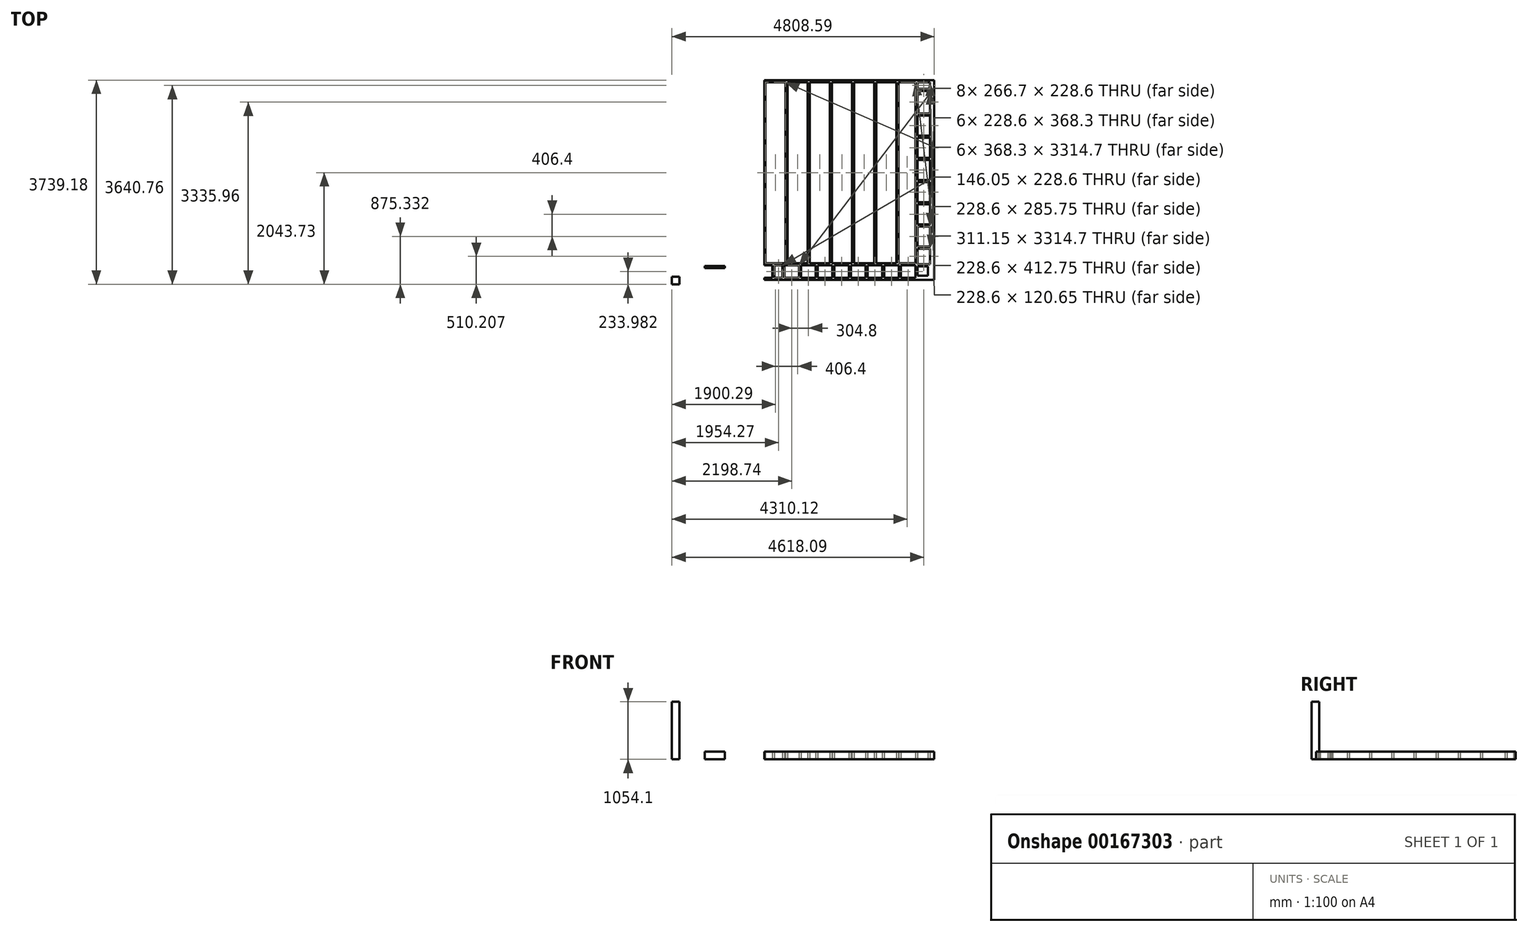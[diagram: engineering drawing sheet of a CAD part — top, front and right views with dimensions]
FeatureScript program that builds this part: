
annotation { "Feature Type Name" : "Feature", "Feature Type Description" : "" }
export const myFeature = defineFeature(function(context is Context, id is Id, definition is map)
    precondition{}
    {
        {
            var Q0;
            Q0=qCreatedBy(makeId("Top.planeOp"),FACE);
            var sketch = newSketch(context, id + "F0", { "sketchPlane" : qUnion([Q0])});
            skLineSegment(sketch, "E0.bottom", {"start": v(-2669.9, 3406.01) * mm, "end": v(403.5, 3406.01) * mm});
            skLineSegment(sketch, "E0.left", {"start": v(-2669.9, 3406.01) * mm, "end": v(-2669.9, 3367.91) * mm});
            skLineSegment(sketch, "E0.right", {"start": v(403.5, 3406.01) * mm, "end": v(403.5, -213.49) * mm});
            skPoint(sketch, "E1.orphan", {"position": v(238.4, 3406.01) * mm});
            skPoint(sketch, "E2.orphan", {"position": v(200.3, 3406.01) * mm});
            skLineSegment(sketch, "E3.0.3.0", {"start": v(136.8, 1170.81) * mm, "end": v(365.4, 1170.81) * mm});
            skLineSegment(sketch, "E3.0.3.1", {"start": v(136.8, 1132.71) * mm, "end": v(365.4, 1132.71) * mm});
            skLineSegment(sketch, "E3.0.4.0", {"start": v(136.8, 1577.21) * mm, "end": v(365.4, 1577.21) * mm});
            skLineSegment(sketch, "E3.0.6.0", {"start": v(136.8, 2390.01) * mm, "end": v(365.4, 2390.01) * mm});
            skLineSegment(sketch, "E3.0.6.1", {"start": v(136.8, 2351.91) * mm, "end": v(365.4, 2351.91) * mm});
            skLineSegment(sketch, "E4", {"start": v(-2669.9, -251.59) * mm, "end": v(403.5, -251.59) * mm});
            skLineSegment(sketch, "E5", {"start": v(-2669.9, -213.49) * mm, "end": v(-2523.85, -213.49) * mm});
            skLineSegment(sketch, "E6.trimOffspring", {"start": v(365.4, 65.91) * mm, "end": v(365.4, 34.16) * mm});
            skLineSegment(sketch, "E7.trimOffspring", {"start": v(136.8, -213.49) * mm, "end": v(403.5, -213.49) * mm});
            skLineSegment(sketch, "E8.trimOffspring", {"start": v(-2669.9, 15.11) * mm, "end": v(-2523.85, 15.11) * mm});
            skLineSegment(sketch, "E9.2.0.0", {"start": v(-1425.3, 15.11) * mm, "end": v(-1425.3, -213.49) * mm});
            skLineSegment(sketch, "E9.2.0.1", {"start": v(-1387.2, 15.11) * mm, "end": v(-1387.2, -213.49) * mm});
            skLineSegment(sketch, "E9.5.0.0", {"start": v(-206.1, 15.11) * mm, "end": v(-206.1, -213.49) * mm});
            skLineSegment(sketch, "E9.5.0.1", {"start": v(-168, 15.11) * mm, "end": v(-168, -213.49) * mm});
            skLineSegment(sketch, "E10.trimOffspring", {"start": v(-1996.8, 15.11) * mm, "end": v(-1730.1, 15.11) * mm});
            skLineSegment(sketch, "E11.trimOffspring", {"start": v(-1387.2, 15.11) * mm, "end": v(-1120.5, 15.11) * mm});
            skLineSegment(sketch, "E12.trimOffspring", {"start": v(-2671, 3367.91) * mm, "end": v(-2669.9, 3367.91) * mm});
            skLineSegment(sketch, "E13.trimOffspring", {"start": v(136.8, -3.94) * mm, "end": v(327.3, -3.94) * mm});
            skLineSegment(sketch, "E14.trimOffspring", {"start": v(365.4, -3.94) * mm, "end": v(365.4, -175.39) * mm});
            skLineSegment(sketch, "E15.trimOffspring", {"start": v(365.4, -213.49) * mm, "end": v(365.4, -213.49) * mm});
            skLineSegment(sketch, "E16.trimOffspring", {"start": v(365.4, -3.94) * mm, "end": v(365.4, -3.94) * mm});
            skLineSegment(sketch, "E17", {"start": v(-1996.8, 15.11) * mm, "end": v(-1996.8, -213.49) * mm});
            skLineSegment(sketch, "E18.trimOffspring", {"start": v(-2339.7, 15.11) * mm, "end": v(-2339.7, -213.49) * mm});
            skLineSegment(sketch, "E19.trimOffspring", {"start": v(-2301.6, 15.11) * mm, "end": v(-2301.6, -213.49) * mm});
            skLineSegment(sketch, "E20.trimOffspring", {"start": v(-2301.6, 15.11) * mm, "end": v(-2034.9, 15.11) * mm});
            skLineSegment(sketch, "E21.trimOffspring", {"start": v(-2034.9, 15.11) * mm, "end": v(-2034.9, -213.49) * mm});
            skLineSegment(sketch, "E22.trimOffspring", {"start": v(-1730.1, 15.11) * mm, "end": v(-1730.1, -213.49) * mm});
            skLineSegment(sketch, "E23.trimOffspring", {"start": v(-1692, 15.11) * mm, "end": v(-1692, -213.49) * mm});
            skLineSegment(sketch, "E24.trimOffspring", {"start": v(-1692, 15.11) * mm, "end": v(-1425.3, 15.11) * mm});
            skLineSegment(sketch, "E25.trimOffspring", {"start": v(-1120.5, 15.11) * mm, "end": v(-1120.5, -213.49) * mm});
            skLineSegment(sketch, "E26.trimOffspring", {"start": v(-1082.4, 15.11) * mm, "end": v(-815.7, 15.11) * mm});
            skLineSegment(sketch, "E27.trimOffspring", {"start": v(-1082.4, 15.11) * mm, "end": v(-1082.4, -213.49) * mm});
            skLineSegment(sketch, "E28.trimOffspring", {"start": v(-815.7, 15.11) * mm, "end": v(-815.7, -213.49) * mm});
            skLineSegment(sketch, "E29.trimOffspring", {"start": v(-777.6, 15.11) * mm, "end": v(-510.9, 15.11) * mm});
            skLineSegment(sketch, "E30.trimOffspring", {"start": v(-777.6, 15.11) * mm, "end": v(-777.6, -213.49) * mm});
            skLineSegment(sketch, "E31.trimOffspring", {"start": v(-510.9, 15.11) * mm, "end": v(-510.9, -213.49) * mm});
            skLineSegment(sketch, "E32.trimOffspring", {"start": v(-472.8, 15.11) * mm, "end": v(-206.1, 15.11) * mm});
            skLineSegment(sketch, "E33.trimOffspring", {"start": v(-472.8, 15.11) * mm, "end": v(-472.8, -213.49) * mm});
            skLineSegment(sketch, "E34.trimOffspring", {"start": v(-168, 15.11) * mm, "end": v(98.7, 15.11) * mm});
            skLineSegment(sketch, "E35.trimOffspring", {"start": v(98.7, 3367.91) * mm, "end": v(98.7, 53.21) * mm});
            skLineSegment(sketch, "E36.trimOffspring", {"start": v(136.8, 2796.41) * mm, "end": v(365.4, 2796.41) * mm});
            skLineSegment(sketch, "E37.trimOffspring", {"start": v(136.8, 2758.31) * mm, "end": v(365.4, 2758.31) * mm});
            skLineSegment(sketch, "E38.trimOffspring", {"start": v(136.8, 3367.91) * mm, "end": v(365.4, 3367.91) * mm});
            skLineSegment(sketch, "E39.trimOffspring", {"start": v(136.8, 3367.91) * mm, "end": v(136.8, 3247.26) * mm});
            skLineSegment(sketch, "E40.trimOffspring", {"start": v(136.8, 1983.61) * mm, "end": v(365.4, 1983.61) * mm});
            skLineSegment(sketch, "E41.trimOffspring", {"start": v(136.8, 1945.51) * mm, "end": v(365.4, 1945.51) * mm});
            skLineSegment(sketch, "E42.trimOffspring", {"start": v(136.8, 1539.11) * mm, "end": v(365.4, 1539.11) * mm});
            skLineSegment(sketch, "E43.trimOffspring", {"start": v(136.8, 1539.11) * mm, "end": v(136.8, 1170.81) * mm});
            skLineSegment(sketch, "E44.trimOffspring", {"start": v(365.4, 1539.11) * mm, "end": v(365.4, 1170.81) * mm});
            skLineSegment(sketch, "E45.trimOffspring", {"start": v(136.8, 1132.71) * mm, "end": v(136.8, 764.41) * mm});
            skLineSegment(sketch, "E46.trimOffspring", {"start": v(136.8, 764.41) * mm, "end": v(365.4, 764.41) * mm});
            skLineSegment(sketch, "E47.trimOffspring", {"start": v(136.8, 726.31) * mm, "end": v(365.4, 726.31) * mm});
            skLineSegment(sketch, "E48.trimOffspring", {"start": v(136.8, 726.31) * mm, "end": v(136.8, 358.01) * mm});
            skLineSegment(sketch, "E49.trimOffspring", {"start": v(136.8, 358.01) * mm, "end": v(365.4, 358.01) * mm});
            skLineSegment(sketch, "E50.trimOffspring", {"start": v(136.8, 319.91) * mm, "end": v(136.8, 53.21) * mm});
            skLineSegment(sketch, "E51.trimOffspring", {"start": v(136.8, 319.91) * mm, "end": v(365.4, 319.91) * mm});
            skLineSegment(sketch, "E52.trimOffspring", {"start": v(136.8, 34.16) * mm, "end": v(365.4, 34.16) * mm});
            skLineSegment(sketch, "E53.trimOffspring", {"start": v(136.8, 65.91) * mm, "end": v(136.8, 34.16) * mm});
            skLineSegment(sketch, "E54.trimOffspring", {"start": v(98.7, 15.11) * mm, "end": v(98.7, -213.49) * mm});
            skLineSegment(sketch, "E55.trimOffspring", {"start": v(136.8, -3.94) * mm, "end": v(136.8, -175.39) * mm});
            skLineSegment(sketch, "E56.trimOffspring", {"start": v(136.8, -213.49) * mm, "end": v(136.8, -213.49) * mm});
            skLineSegment(sketch, "E57.trimOffspring", {"start": v(365.4, 319.91) * mm, "end": v(365.4, 53.21) * mm});
            skLineSegment(sketch, "E58.trimOffspring", {"start": v(365.4, 726.31) * mm, "end": v(365.4, 358.01) * mm});
            skLineSegment(sketch, "E59.trimOffspring", {"start": v(365.4, 1132.71) * mm, "end": v(365.4, 764.41) * mm});
            skLineSegment(sketch, "E60.trimOffspring", {"start": v(365.4, 1945.51) * mm, "end": v(365.4, 1577.21) * mm});
            skLineSegment(sketch, "E61.trimOffspring", {"start": v(365.4, 2351.91) * mm, "end": v(365.4, 1983.61) * mm});
            skLineSegment(sketch, "E62.trimOffspring", {"start": v(365.4, 2758.31) * mm, "end": v(365.4, 2390.01) * mm});
            skLineSegment(sketch, "E63.trimOffspring", {"start": v(365.4, 3367.91) * mm, "end": v(365.4, 3247.26) * mm});
            skLineSegment(sketch, "E64.trimOffspring", {"start": v(-168, -213.49) * mm, "end": v(98.7, -213.49) * mm});
            skLineSegment(sketch, "E65.trimOffspring", {"start": v(-472.8, -213.49) * mm, "end": v(-206.1, -213.49) * mm});
            skLineSegment(sketch, "E66.trimOffspring", {"start": v(-777.6, -213.49) * mm, "end": v(-510.9, -213.49) * mm});
            skLineSegment(sketch, "E67.trimOffspring", {"start": v(-1082.4, -213.49) * mm, "end": v(-815.7, -213.49) * mm});
            skLineSegment(sketch, "E68.trimOffspring", {"start": v(-1387.2, -213.49) * mm, "end": v(-1120.5, -213.49) * mm});
            skLineSegment(sketch, "E69.trimOffspring", {"start": v(-1692, -213.49) * mm, "end": v(-1425.3, -213.49) * mm});
            skLineSegment(sketch, "E70.trimOffspring", {"start": v(-2301.6, -213.49) * mm, "end": v(-2034.9, -213.49) * mm});
            skLineSegment(sketch, "E71.trimOffspring", {"start": v(-2523.85, -213.49) * mm, "end": v(-2339.7, -213.49) * mm});
            skLineSegment(sketch, "E72.trimOffspring", {"start": v(-1996.8, -213.49) * mm, "end": v(-1730.1, -213.49) * mm});
            skLineSegment(sketch, "E73.trimOffspring", {"start": v(136.8, 3209.16) * mm, "end": v(365.4, 3209.16) * mm});
            skPoint(sketch, "E74.orphan", {"position": v(149.5, 3367.91) * mm});
            skLineSegment(sketch, "E75.trimOffspring", {"start": v(136.8, 3247.26) * mm, "end": v(365.4, 3247.26) * mm});
            skLineSegment(sketch, "E76.trimOffspring", {"start": v(136.8, 3209.16) * mm, "end": v(136.8, 2390.01) * mm});
            skLineSegment(sketch, "E77.trimOffspring", {"start": v(365.4, 3209.16) * mm, "end": v(365.4, 2796.41) * mm});
            skLineSegment(sketch, "E78.trimOffspring", {"start": v(136.8, 2351.91) * mm, "end": v(136.8, 1983.61) * mm});
            skLineSegment(sketch, "E79.trimOffspring", {"start": v(136.8, 1945.51) * mm, "end": v(136.8, 1577.21) * mm});
            skLineSegment(sketch, "E80.0", {"start": v(327.3, -3.94) * mm, "end": v(327.3, -175.39) * mm});
            skLineSegment(sketch, "E81.0", {"start": v(136.8, -175.39) * mm, "end": v(327.3, -175.39) * mm});
            skLineSegment(sketch, "E82.0", {"start": v(136.8, -213.49) * mm, "end": v(365.4, -213.49) * mm});
            skLineSegment(sketch, "E83.trimOffspring", {"start": v(365.4, -175.39) * mm, "end": v(365.4, -175.39) * mm});
            skLineSegment(sketch, "E84.trimOffspring", {"start": v(-2485.75, 15.11) * mm, "end": v(-2339.7, 15.11) * mm});
            skLineSegment(sketch, "E85.trimOffspring", {"start": v(-2485.75, 15.11) * mm, "end": v(-2485.75, -213.49) * mm});
            skLineSegment(sketch, "E86.trimOffspring", {"start": v(-2523.85, 15.11) * mm, "end": v(-2523.85, -213.49) * mm});
            skLineSegment(sketch, "E87", {"start": v(-2669.9, -213.49) * mm, "end": v(-2669.9, -251.59) * mm});
            skLineSegment(sketch, "E88", {"start": v(-2669.9, 53.21) * mm, "end": v(-2669.9, 15.11) * mm});
            skLineSegment(sketch, "E89.0", {"start": v(441.6, 3406.01) * mm, "end": v(441.6, -251.59) * mm});
            skLineSegment(sketch, "E90", {"start": v(403.5, 3406.01) * mm, "end": v(441.6, 3406.01) * mm});
            skLineSegment(sketch, "E91", {"start": v(403.5, -251.59) * mm, "end": v(441.6, -251.59) * mm});
            skLineSegment(sketch, "E92.0", {"start": v(-2671, 3406.01) * mm, "end": v(-2671, 3367.91) * mm});
            skLineSegment(sketch, "E93.0", {"start": v(-2650.85, 3367.91) * mm, "end": v(-2650.85, 53.21) * mm});
            skLineSegment(sketch, "E94", {"start": v(-2669.9, 53.21) * mm, "end": v(-2669.9, 3367.91) * mm});
            skLineSegment(sketch, "E95.trimOffspring", {"start": v(-2650.85, 3367.91) * mm, "end": v(-2282.55, 3367.91) * mm});
            skLineSegment(sketch, "E96", {"start": v(98.7, 53.21) * mm, "end": v(-2650.85, 53.21) * mm});
            skPoint(sketch, "E97.orphan", {"position": v(-2650.85, 15.11) * mm});
            skLineSegment(sketch, "E98.0", {"start": v(-2244.45, 3367.91) * mm, "end": v(-2244.45, 53.21) * mm});
            skLineSegment(sketch, "E99.0", {"start": v(-2282.55, 3367.91) * mm, "end": v(-2282.55, 53.21) * mm});
            skLineSegment(sketch, "E100.1.0.0", {"start": v(-1838.05, 3367.91) * mm, "end": v(-1838.05, 53.21) * mm});
            skLineSegment(sketch, "E100.1.0.1", {"start": v(-1876.15, 3367.91) * mm, "end": v(-1876.15, 53.21) * mm});
            skLineSegment(sketch, "E100.2.0.0", {"start": v(-1431.65, 3367.91) * mm, "end": v(-1431.65, 53.21) * mm});
            skLineSegment(sketch, "E100.2.0.1", {"start": v(-1469.75, 3367.91) * mm, "end": v(-1469.75, 53.21) * mm});
            skLineSegment(sketch, "E100.3.0.0", {"start": v(-1025.25, 3367.91) * mm, "end": v(-1025.25, 53.21) * mm});
            skLineSegment(sketch, "E100.3.0.1", {"start": v(-1063.35, 3367.91) * mm, "end": v(-1063.35, 53.21) * mm});
            skLineSegment(sketch, "E100.4.0.0", {"start": v(-618.85, 3367.91) * mm, "end": v(-618.85, 53.21) * mm});
            skLineSegment(sketch, "E100.4.0.1", {"start": v(-656.95, 3367.91) * mm, "end": v(-656.95, 53.21) * mm});
            skLineSegment(sketch, "E100.5.0.0", {"start": v(-212.45, 3367.91) * mm, "end": v(-212.45, 53.21) * mm});
            skLineSegment(sketch, "E100.5.0.1", {"start": v(-250.55, 3367.91) * mm, "end": v(-250.55, 53.21) * mm});
            skLineSegment(sketch, "E100.direction1", {"start": v(-2282.55, 53.21) * mm, "end": v(-1876.15, 53.21) * mm, "construction": true});
            skLineSegment(sketch, "E101.trimOffspring", {"start": v(-2244.45, 3367.91) * mm, "end": v(-1876.15, 3367.91) * mm});
            skLineSegment(sketch, "E102.trimOffspring", {"start": v(-1838.05, 3367.91) * mm, "end": v(-1469.75, 3367.91) * mm});
            skLineSegment(sketch, "E103.trimOffspring", {"start": v(-1431.65, 3367.91) * mm, "end": v(-1063.35, 3367.91) * mm});
            skLineSegment(sketch, "E104.trimOffspring", {"start": v(-1025.25, 3367.91) * mm, "end": v(-656.95, 3367.91) * mm});
            skLineSegment(sketch, "E105.trimOffspring", {"start": v(-618.85, 3367.91) * mm, "end": v(-250.55, 3367.91) * mm});
            skLineSegment(sketch, "E106.trimOffspring", {"start": v(-212.45, 3367.91) * mm, "end": v(98.7, 3367.91) * mm});
            skSolve(sketch);
        }
        {
            var Q0;
            {var subQ0=sQuery(id+"F0.wireOp",EDGE,"b4387343-3526-4506-bbcd-7e7664f48f6e.trimOffspring");Q0=makeQuery(id+"F0.imprint","IMPRINT",FACE,{"disambiguationData":[TD([[makeQuery(id+"F0.imprint","IMPRINT",EDGE,{"derivedFrom":subQ0}),1.0]])]});}
            var Q1;
            {var subQ0=sQuery(id+"F0.wireOp",EDGE,"E3.0.1.0");Q1=makeQuery(id+"F0.imprint","IMPRINT",FACE,{"disambiguationData":[TD([[makeQuery(id+"F0.imprint","IMPRINT",EDGE,{"derivedFrom":subQ0}),-1.0]])]});}
            var Q2;
            {var subQ0=sQuery(id+"F0.wireOp",EDGE,"E3.0.2.0");Q2=makeQuery(id+"F0.imprint","IMPRINT",FACE,{"disambiguationData":[TD([[makeQuery(id+"F0.imprint","IMPRINT",EDGE,{"derivedFrom":subQ0}),-1.0]])]});}
            var Q3;
            {var subQ0=sQuery(id+"F0.wireOp",EDGE,"E3.0.3.0");Q3=makeQuery(id+"F0.imprint","IMPRINT",FACE,{"disambiguationData":[TD([[makeQuery(id+"F0.imprint","IMPRINT",EDGE,{"derivedFrom":subQ0}),-1.0]])]});}
            var Q4;
            {var subQ0=sQuery(id+"F0.wireOp",EDGE,"E3.0.4.0");Q4=makeQuery(id+"F0.imprint","IMPRINT",FACE,{"disambiguationData":[TD([[makeQuery(id+"F0.imprint","IMPRINT",EDGE,{"derivedFrom":subQ0}),-1.0]])]});}
            var Q5;
            {var subQ0=sQuery(id+"F0.wireOp",EDGE,"E3.0.5.0");Q5=makeQuery(id+"F0.imprint","IMPRINT",FACE,{"disambiguationData":[TD([[makeQuery(id+"F0.imprint","IMPRINT",EDGE,{"derivedFrom":subQ0}),-1.0]])]});}
            var Q6;
            {var subQ0=sQuery(id+"F0.wireOp",EDGE,"E3.0.6.0");Q6=makeQuery(id+"F0.imprint","IMPRINT",FACE,{"disambiguationData":[TD([[makeQuery(id+"F0.imprint","IMPRINT",EDGE,{"derivedFrom":subQ0}),-1.0]])]});}
            var Q7;
            {var subQ0=sQuery(id+"F0.wireOp",EDGE,"E3.0.7.0");Q7=makeQuery(id+"F0.imprint","IMPRINT",FACE,{"disambiguationData":[TD([[makeQuery(id+"F0.imprint","IMPRINT",EDGE,{"derivedFrom":subQ0}),-1.0]])]});}
            var Q8;
            {var subQ0=sQuery(id+"F0.wireOp",EDGE,"E3.0.8.0");Q8=makeQuery(id+"F0.imprint","IMPRINT",FACE,{"disambiguationData":[TD([[makeQuery(id+"F0.imprint","IMPRINT",EDGE,{"derivedFrom":subQ0}),-1.0]])]});}
            var Q9;
            Q9=makeQuery(id+"F0.imprint","IMPRINT",FACE,{"disambiguationData":[TD([[makeQuery(id+"F0.imprint","IMPRINT",EDGE,{"derivedFrom":sQuery(id+"F0.wireOp",EDGE,"E0.top")}),1.0]])]});
            var Q10;
            Q10=makeQuery(id+"F0.imprint","IMPRINT",FACE,{"disambiguationData":[TD([[makeQuery(id+"F0.imprint","IMPRINT",EDGE,{"derivedFrom":sQuery(id+"F0.wireOp",EDGE,"E0.top")}),1.0]])]});
            var Q11;
            Q11=makeQuery(id+"F0.imprint","IMPRINT",FACE,{"disambiguationData":[TD([[makeQuery(id+"F0.imprint","IMPRINT",EDGE,{"derivedFrom":sQuery(id+"F0.wireOp",EDGE,"E0.top")}),1.0]])]});
            var Q12;
            Q12=makeQuery(id+"F0.imprint","IMPRINT",FACE,{"disambiguationData":[TD([[makeQuery(id+"F0.imprint","IMPRINT",EDGE,{"derivedFrom":sQuery(id+"F0.wireOp",EDGE,"E0.top")}),1.0]])]});
            var Q13;
            {var subQ26=sQuery(id+"F0.wireOp",EDGE,"725c7f7c-71b0-4347-98c5-58dc943cd30f.trimOffspring");Q13=makeQuery(id+"F0.imprint","IMPRINT",FACE,{"disambiguationData":[TD([[makeQuery(id+"F0.imprint","IMPRINT",EDGE,{"derivedFrom":subQ26}),-1.0]])]});}
            var Q14;
            {var subQ0=sQuery(id+"F0.wireOp",EDGE,"51c1605e-bbe8-4e2b-b86c-3fa6e730653b.trimOffspring");Q14=makeQuery(id+"F0.imprint","IMPRINT",FACE,{"disambiguationData":[TD([[makeQuery(id+"F0.imprint","IMPRINT",EDGE,{"derivedFrom":subQ0}),1.0]])]});}
            var Q15;
            {var subQ26=sQuery(id+"F0.wireOp",EDGE,"725c7f7c-71b0-4347-98c5-58dc943cd30f.trimOffspring");Q15=makeQuery(id+"F0.imprint","IMPRINT",FACE,{"disambiguationData":[TD([[makeQuery(id+"F0.imprint","IMPRINT",EDGE,{"derivedFrom":subQ26}),-1.0]])]});}
            var Q16;
            Q16=makeQuery(id+"F0.imprint","IMPRINT",FACE,{"disambiguationData":[TD([[makeQuery(id+"F0.imprint","IMPRINT",EDGE,{"derivedFrom":sQuery(id+"F0.wireOp",EDGE,"E0.top")}),1.0]])]});
            var Q17;
            Q17=makeQuery(id+"F0.imprint","IMPRINT",FACE,{"disambiguationData":[TD([[makeQuery(id+"F0.imprint","IMPRINT",EDGE,{"derivedFrom":sQuery(id+"F0.wireOp",EDGE,"E0.top")}),1.0]])]});
            var Q18;
            {var subQ0=sQuery(id+"F0.wireOp",EDGE,"E3.0.8.0");Q18=makeQuery(id+"F0.imprint","IMPRINT",FACE,{"disambiguationData":[TD([[makeQuery(id+"F0.imprint","IMPRINT",EDGE,{"derivedFrom":subQ0}),-1.0]])]});}
            var Q19;
            {var subQ0=sQuery(id+"F0.wireOp",EDGE,"E3.0.7.0");Q19=makeQuery(id+"F0.imprint","IMPRINT",FACE,{"disambiguationData":[TD([[makeQuery(id+"F0.imprint","IMPRINT",EDGE,{"derivedFrom":subQ0}),-1.0]])]});}
            var Q20;
            {var subQ0=sQuery(id+"F0.wireOp",EDGE,"E3.0.6.0");Q20=makeQuery(id+"F0.imprint","IMPRINT",FACE,{"disambiguationData":[TD([[makeQuery(id+"F0.imprint","IMPRINT",EDGE,{"derivedFrom":subQ0}),-1.0]])]});}
            var Q21;
            {var subQ0=sQuery(id+"F0.wireOp",EDGE,"E3.0.5.0");Q21=makeQuery(id+"F0.imprint","IMPRINT",FACE,{"disambiguationData":[TD([[makeQuery(id+"F0.imprint","IMPRINT",EDGE,{"derivedFrom":subQ0}),-1.0]])]});}
            var Q22;
            {var subQ0=sQuery(id+"F0.wireOp",EDGE,"E3.0.4.0");Q22=makeQuery(id+"F0.imprint","IMPRINT",FACE,{"disambiguationData":[TD([[makeQuery(id+"F0.imprint","IMPRINT",EDGE,{"derivedFrom":subQ0}),-1.0]])]});}
            var Q23;
            {var subQ0=sQuery(id+"F0.wireOp",EDGE,"E3.0.3.0");Q23=makeQuery(id+"F0.imprint","IMPRINT",FACE,{"disambiguationData":[TD([[makeQuery(id+"F0.imprint","IMPRINT",EDGE,{"derivedFrom":subQ0}),-1.0]])]});}
            var Q24;
            {var subQ0=sQuery(id+"F0.wireOp",EDGE,"E3.0.2.0");Q24=makeQuery(id+"F0.imprint","IMPRINT",FACE,{"disambiguationData":[TD([[makeQuery(id+"F0.imprint","IMPRINT",EDGE,{"derivedFrom":subQ0}),-1.0]])]});}
            var Q25;
            {var subQ0=sQuery(id+"F0.wireOp",EDGE,"E3.0.1.0");Q25=makeQuery(id+"F0.imprint","IMPRINT",FACE,{"disambiguationData":[TD([[makeQuery(id+"F0.imprint","IMPRINT",EDGE,{"derivedFrom":subQ0}),-1.0]])]});}
            var Q26;
            {var subQ0=sQuery(id+"F0.wireOp",EDGE,"eb889cc4-fd61-4203-853b-da0059d36901.trimOffspring");Q26=makeQuery(id+"F0.imprint","IMPRINT",FACE,{"disambiguationData":[TD([[makeQuery(id+"F0.imprint","IMPRINT",EDGE,{"derivedFrom":subQ0}),-1.0]])]});}
            var Q27;
            {var subQ0=sQuery(id+"F0.wireOp",EDGE,"496921f4-0462-4830-be14-b69f4c9a3ac6.0");Q27=makeQuery(id+"F0.imprint","IMPRINT",FACE,{"disambiguationData":[TD([[makeQuery(id+"F0.imprint","IMPRINT",EDGE,{"derivedFrom":subQ0}),1.0]])]});}
            extrude(context, id + "F1", {"entities" : qUnion([Q0, Q1, Q2, Q3, Q4, Q5, Q6, Q7, Q8, Q9, Q10, Q11, Q12, Q13, Q14, Q15, Q16, Q17, Q18, Q19, Q20, Q21, Q22, Q23, Q24, Q25, Q26, Q27]), "depth" : 139.7 * mm});
        }
        {
            var Q0;
            Q0=qCreatedBy(makeId("Top.planeOp"),FACE);
            var sketch = newSketch(context, id + "F2", { "sketchPlane" : qUnion([Q0])});
            skLineSegment(sketch, "E107.bottom", {"start": v(-4366.99, -193.47) * mm, "end": v(-4227.29, -193.47) * mm});
            skLineSegment(sketch, "E107.top", {"start": v(-4366.99, -333.17) * mm, "end": v(-4227.29, -333.17) * mm});
            skLineSegment(sketch, "E107.left", {"start": v(-4366.99, -193.47) * mm, "end": v(-4366.99, -333.17) * mm});
            skLineSegment(sketch, "E107.right", {"start": v(-4227.29, -193.47) * mm, "end": v(-4227.29, -333.17) * mm});
            skSolve(sketch);
        }
        {
            var Q0;
            Q0 = qSketchRegion(id + "F2", true);
            extrude(context, id + "F3", {"entities" : qUnion([Q0]), "depth" : 1054.1 * mm});
        }
        {
            var Q0;
            Q0=qCreatedBy(makeId("Front.planeOp"),FACE);
            var sketch = newSketch(context, id + "F4", { "sketchPlane" : qUnion([Q0])});
            skLineSegment(sketch, "E108.bottom", {"start": v(-3765.96, 139.7) * mm, "end": v(-3397.66, 139.7) * mm});
            skLineSegment(sketch, "E108.top", {"start": v(-3765.96, 0) * mm, "end": v(-3397.66, 0) * mm});
            skLineSegment(sketch, "E108.left", {"start": v(-3765.96, 139.7) * mm, "end": v(-3765.96, 0) * mm});
            skLineSegment(sketch, "E108.right", {"start": v(-3397.66, 139.7) * mm, "end": v(-3397.66, 0) * mm});
            skSolve(sketch);
        }
        {
            var Q0;
            Q0 = qSketchRegion(id + "F4", true);
            extrude(context, id + "F5", {"entities" : qUnion([Q0]), "depth" : 38.1 * mm});
        }
    });
